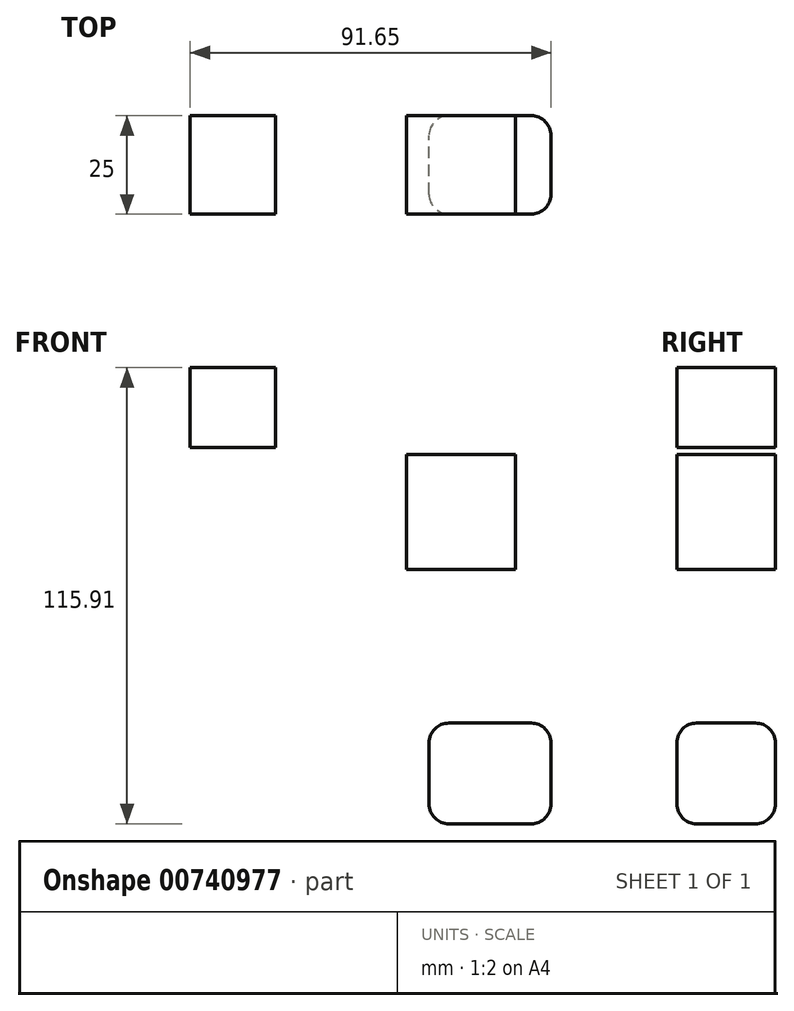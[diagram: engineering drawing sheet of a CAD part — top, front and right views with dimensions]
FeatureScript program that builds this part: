
annotation { "Feature Type Name" : "Feature", "Feature Type Description" : "" }
export const myFeature = defineFeature(function(context is Context, id is Id, definition is map)
    precondition{}
    {
        {
            var Q0;
            Q0=qCreatedBy(makeId("Front.planeOp"),FACE);
            var sketch = newSketch(context, id + "F0", { "sketchPlane" : qUnion([Q0])});
            skLineSegment(sketch, "E0.bottom", {"start": v(-38.97, 56.29) * mm, "end": v(-17.23, 56.29) * mm});
            skLineSegment(sketch, "E0.top", {"start": v(-38.97, 36.05) * mm, "end": v(-17.23, 36.05) * mm});
            skLineSegment(sketch, "E0.left", {"start": v(-38.97, 56.29) * mm, "end": v(-38.97, 36.05) * mm});
            skLineSegment(sketch, "E0.right", {"start": v(-17.23, 56.29) * mm, "end": v(-17.23, 36.05) * mm});
            skLineSegment(sketch, "E1.bottom", {"start": v(16.06, 34.2) * mm, "end": v(43.65, 34.2) * mm});
            skLineSegment(sketch, "E1.top", {"start": v(16.06, 4.94) * mm, "end": v(43.65, 4.94) * mm});
            skLineSegment(sketch, "E1.left", {"start": v(16.06, 34.2) * mm, "end": v(16.06, 4.94) * mm});
            skLineSegment(sketch, "E1.right", {"start": v(43.65, 34.2) * mm, "end": v(43.65, 4.94) * mm});
            skLineSegment(sketch, "E2.bottom", {"start": v(-34.45, -33.36) * mm, "end": v(-10.37, -33.36) * mm});
            skLineSegment(sketch, "E2.top", {"start": v(-34.45, -49.58) * mm, "end": v(-10.37, -49.58) * mm});
            skLineSegment(sketch, "E2.left", {"start": v(-34.45, -33.36) * mm, "end": v(-34.45, -49.58) * mm});
            skLineSegment(sketch, "E2.right", {"start": v(-10.37, -33.36) * mm, "end": v(-10.37, -49.58) * mm});
            skLineSegment(sketch, "E3.bottom", {"start": v(21.74, -34.03) * mm, "end": v(52.68, -34.03) * mm});
            skLineSegment(sketch, "E3.top", {"start": v(21.74, -59.62) * mm, "end": v(52.68, -59.62) * mm});
            skLineSegment(sketch, "E3.left", {"start": v(21.74, -34.03) * mm, "end": v(21.74, -59.62) * mm});
            skLineSegment(sketch, "E3.right", {"start": v(52.68, -34.03) * mm, "end": v(52.68, -59.62) * mm});
            skSolve(sketch);
        }
        {
            var Q0;
            Q0 = qSketchRegion(id + "F0", true);
            extrude(context, id + "F1", {"entities" : qUnion([Q0]), "depth" : 25 * mm, "offsetDistance" : 25 * mm});
        }
        {
            var Q0;
            Q0=makeQuery(id+"F1.opExtrude","SWEPT_BODY",BODY,{"disambiguationData":[OSD([sQuery(id+"F0.wireOp",EDGE,"E2.bottom"),sQuery(id+"F0.wireOp",EDGE,"E2.top"),sQuery(id+"F0.wireOp",EDGE,"E2.left"),sQuery(id+"F0.wireOp",EDGE,"E2.right")])]});
            deleteBodies(context, id + "F2", {"entities" : qUnion([Q0])});
        }
        {
            var Q0;
            Q0=makeQuery(id+"F1.opExtrude","CAP_EDGE",EDGE,{"disambiguationData":[OSD([sQuery(id+"F0.wireOp",EDGE,"E3.top")])],"isStart":false});
            var Q1;
            Q1=makeQuery(id+"F1.opExtrude","CAP_EDGE",EDGE,{"disambiguationData":[OSD([sQuery(id+"F0.wireOp",EDGE,"E3.right")])],"isStart":false});
            var Q2;
            Q2=makeQuery(id+"F1.opExtrude","CAP_EDGE",EDGE,{"disambiguationData":[OSD([sQuery(id+"F0.wireOp",EDGE,"E3.bottom")])],"isStart":false});
            var Q3;
            Q3=makeQuery(id+"F1.opExtrude","CAP_EDGE",EDGE,{"disambiguationData":[OSD([sQuery(id+"F0.wireOp",EDGE,"E3.top")])],"isStart":true});
            var Q4;
            Q4=makeQuery(id+"F1.opExtrude","CAP_EDGE",EDGE,{"disambiguationData":[OSD([sQuery(id+"F0.wireOp",EDGE,"E3.left")])],"isStart":false});
            var Q5;
            Q5=makeQuery(id+"F1.opExtrude","SWEPT_EDGE",EDGE,{"disambiguationData":[OSD([sQuery(id+"F0.wireOp",EDGE,"E3.bottom"),sQuery(id+"F0.wireOp",EDGE,"E3.right")])]});
            var Q6;
            Q6=makeQuery(id+"F1.opExtrude","CAP_EDGE",EDGE,{"disambiguationData":[OSD([sQuery(id+"F0.wireOp",EDGE,"E3.bottom")])],"isStart":true});
            var Q7;
            Q7=makeQuery(id+"F1.opExtrude","SWEPT_EDGE",EDGE,{"disambiguationData":[OSD([sQuery(id+"F0.wireOp",EDGE,"E3.top"),sQuery(id+"F0.wireOp",EDGE,"E3.right")])]});
            var Q8;
            Q8=makeQuery(id+"F1.opExtrude","CAP_EDGE",EDGE,{"disambiguationData":[OSD([sQuery(id+"F0.wireOp",EDGE,"E3.right")])],"isStart":true});
            var Q9;
            Q9=makeQuery(id+"F1.opExtrude","CAP_EDGE",EDGE,{"disambiguationData":[OSD([sQuery(id+"F0.wireOp",EDGE,"E3.left")])],"isStart":true});
            var Q10;
            Q10=makeQuery(id+"F1.opExtrude","SWEPT_EDGE",EDGE,{"disambiguationData":[OSD([sQuery(id+"F0.wireOp",EDGE,"E3.top"),sQuery(id+"F0.wireOp",EDGE,"E3.left")])]});
            var Q11;
            Q11=makeQuery(id+"F1.opExtrude","SWEPT_EDGE",EDGE,{"disambiguationData":[OSD([sQuery(id+"F0.wireOp",EDGE,"E3.bottom"),sQuery(id+"F0.wireOp",EDGE,"E3.left")])]});
            fillet(context, id + "F3", {"entities" : qUnion([Q0, Q1, Q2, Q3, Q4, Q5, Q6, Q7, Q8, Q9, Q10, Q11]), "radius" : 5 * mm, "tangentPropagation" : true, "allowEdgeOverflow" : false});
        }
    });
